# Revit family: HERZ-TS-90-V Thermostatic Valve Reverse Angle Model 7728
name_source: partatom
category: Rohrzubehör
units: mm (PartAtom-declared; Revit-internal decimal feet)

## family parameters
Arbeitsebenenbasiert = Nein
Beim Laden mit Abzugskörper schneiden = Nein
Bemaßung runder Anschluss = Durchmesser verwenden
Gemeinsam genutzt = Nein
Immer vertikal = Ja
OmniClass-Nummer = 23.65.55.14
OmniClass-Titel = Valves for Liquid Services
Teiletyp = Unterbricht

## types (16) — shared parameters
Application = Water heating systems in which hydraulic balancing via return valves is not possible or not desired.
Body = nickel plated
Connection thread for thermostatic head = M28x1.5
Hersteller = HERZ Armaturen Ges.m.b.H.
L04 = 3.5 mm  [stored 0.0114829 ft]
LO1 = 16 mm  [stored 0.0524934 ft]
Max. operating pressure = 1000000.0 Pa
Max. operating temperature = 110 °C
Medium = Heating water purity according to Austrian standard ÖNORM H 5195 and/or VDI-guideline 2035.
Model = All models are nickel plated and supplied with a red screw cap.
R05 = 4 mm  [stored 0.0131234 ft]
S01 = 10 mm  [stored 0.0328084 ft]
SCRNCODE = 05;00;02
SCRNSEQ = ARM;ARM_TYP="ALLF";2
Screw cap = plastic, red
zero-valued in all types: Vorgabe-Ansicht

## per-type parameters (varying)
| type | Part number TH | TH_Kopf_7230 | TH_Kopf_7260 | TH_Kopf_9200_03 | TH_Kopf_9200_06 | TH_Kopf_9200_13 | TH_Kopf_9200_16 | TH_Kopf_9200_30 | TH_Kopf_9200_60 | TH_Kopf_9230 | TH_Kopf_9260 | TH_Kopf_9330_10000mm | TH_Kopf_9330_2000mm | TH_Kopf_9330_5000mm | TH_Kopf_9330_8000mm | TH_Kopf_9860 | URL |
| without thermostatic head | 0 | Nein | Nein | Nein | Nein | Nein | Nein | Nein | Nein | Nein | Nein | Nein | Nein | Nein | Nein | Nein | www.herzvalves.com |
| with thermostatic head_7230 | 1723006 | Ja | Nein | Nein | Nein | Nein | Nein | Nein | Nein | Nein | Nein | Nein | Nein | Nein | Nein | Nein | www.herzvalves.com |
| with thermostatic head_7260 | 1726006 | Nein | Ja | Nein | Nein | Nein | Nein | Nein | Nein | Nein | Nein | Nein | Nein | Nein | Nein | Nein | www.herzvalves.com |
| with thermostatic head_9200_03 | 1920003 | Nein | Nein | Ja | Nein | Nein | Nein | Nein | Nein | Nein | Nein | Nein | Nein | Nein | Nein | Nein | www.herzvalves.com |
| with thermostatic head_9200_06 | 1920006 | Nein | Nein | Nein | Ja | Nein | Nein | Nein | Nein | Nein | Nein | Nein | Nein | Nein | Nein | Nein | www.herzvalves.com |
| with thermostatic head_9200_13 | 1920013 | Nein | Nein | Nein | Nein | Ja | Nein | Nein | Nein | Nein | Nein | Nein | Nein | Nein | Nein | Nein | www.herzvalves.com |
| with thermostatic head_9200_16 | 1920016 | Nein | Nein | Nein | Nein | Nein | Ja | Nein | Nein | Nein | Nein | Nein | Nein | Nein | Nein | Nein | www.herzvalves.com |
| with thermostatic head_9200_30 | 1920030 | Nein | Nein | Nein | Nein | Nein | Nein | Ja | Nein | Nein | Nein | Nein | Nein | Nein | Nein | Nein | www.herz-armaturen.at |
| with thermostatic head_9200_60 | 1920060 | Nein | Nein | Nein | Nein | Nein | Nein | Nein | Ja | Nein | Nein | Nein | Nein | Nein | Nein | Nein | www.herzvalves.com |
| with thermostatic head_9230 | 1923006 | Nein | Nein | Nein | Nein | Nein | Nein | Nein | Nein | Ja | Nein | Nein | Nein | Nein | Nein | Nein | www.herzvalves.com |
| with thermostatic head_9260 | 1926006 | Nein | Nein | Nein | Nein | Nein | Nein | Nein | Nein | Nein | Ja | Nein | Nein | Nein | Nein | Nein | www.herzvalves.com |
| with thermostatic head_9330_10000mm | 1933020 | Nein | Nein | Nein | Nein | Nein | Nein | Nein | Nein | Nein | Nein | Ja | Nein | Nein | Nein | Nein | www.herzvalves.com |
| with thermostatic head_9330_2000mm | 1933005 | Nein | Nein | Nein | Nein | Nein | Nein | Nein | Nein | Nein | Nein | Nein | Ja | Nein | Nein | Nein | www.herzvalves.com |
| with thermostatic head_9330_5000mm | 1933010 | Nein | Nein | Nein | Nein | Nein | Nein | Nein | Nein | Nein | Nein | Nein | Nein | Ja | Nein | Nein | www.herzvalves.com |
| with thermostatic head_9330_8000mm | 1933018 | Nein | Nein | Nein | Nein | Nein | Nein | Nein | Nein | Nein | Nein | Nein | Nein | Nein | Ja | Nein | www.herzvalves.com |
| with thermostatic head_9860 | 1986010 | Nein | Nein | Nein | Nein | Nein | Nein | Nein | Nein | Nein | Nein | Nein | Nein | Nein | Nein | Ja | www.herzvalves.com |

note: [stored X ft] marks values corroborated as IEEE doubles in the binary element streams (Revit-internal decimal feet)
